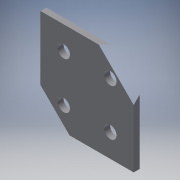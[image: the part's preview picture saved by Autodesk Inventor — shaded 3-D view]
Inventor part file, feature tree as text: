
AUTODESK INVENTOR PART (.ipt)
format: ipt  version: 2016 (Build 200138000, 138)  size: 107,520 bytes
history: native  units: in
note: dims shown in document units (in); Inventor stores cm internally (conversion verified against a paired STEP export)
features: extrude x1, sketch x1
ambient origin geometry x8: Origin, YZ Plane, XZ Plane, XY Plane, X Axis, Y Axis, Z Axis, Center Point
bodies: Body1 (feature_tree)
feature tree (2):
  extrude  "Extrusion2"  Depth=0.125in
  sketch  "Sketch1"  dims[d0=2.0in d1=1.0in d2=3.0in d3=2.0in d4=0.2656in d5=1.5in d6=0.5in d7=1.5in d9=0.5in d10=0.5in d14=0.5in d15=0.5in d16=0.125in d17=0.0in d18=0.5in]
